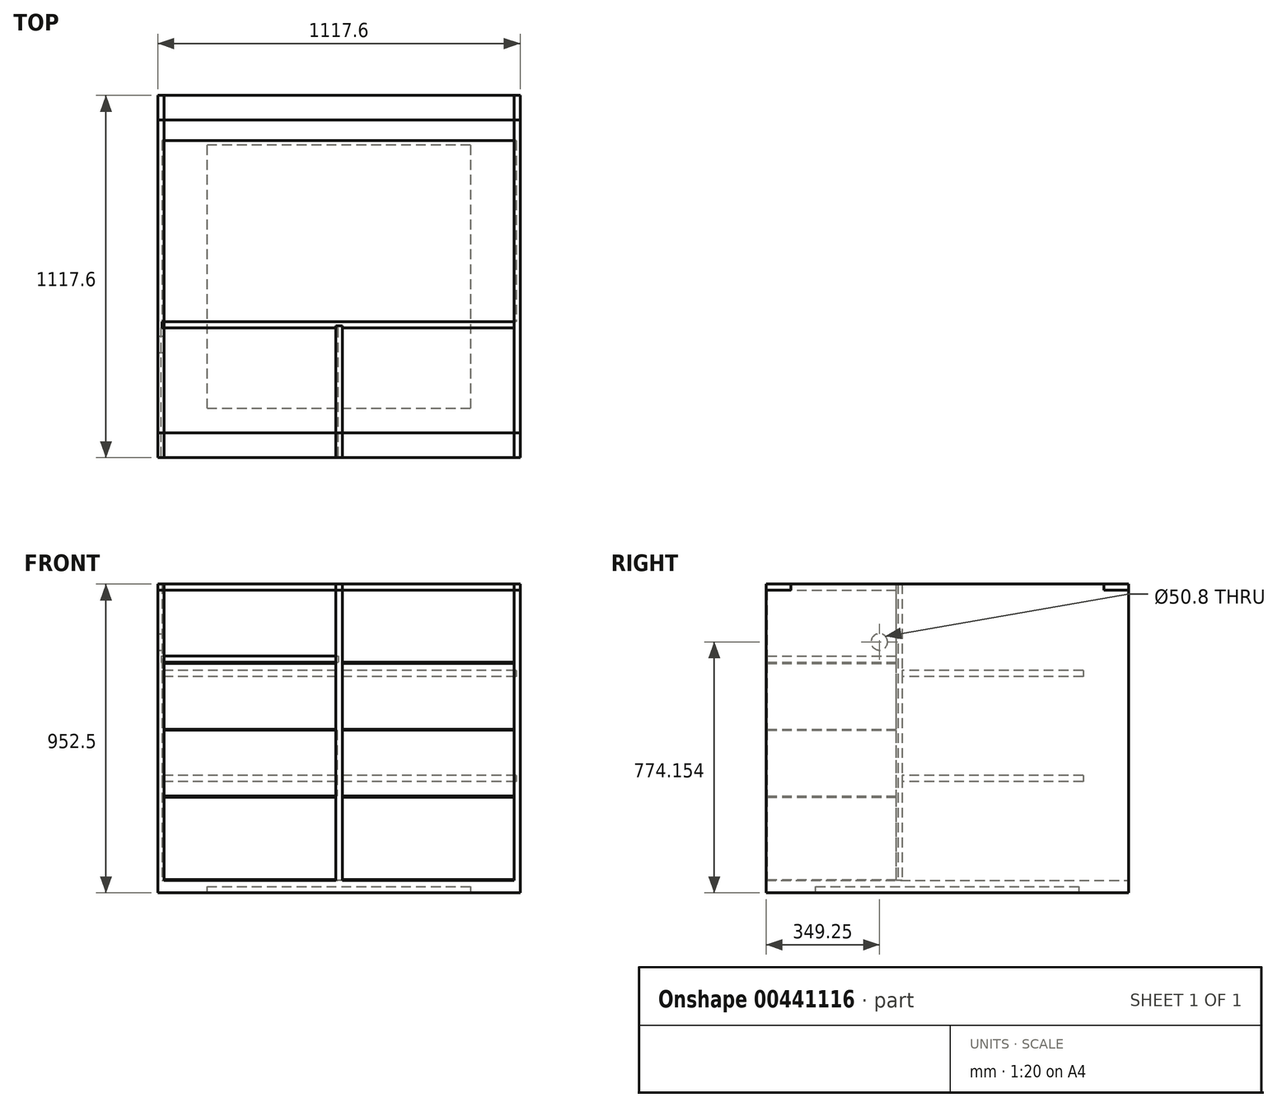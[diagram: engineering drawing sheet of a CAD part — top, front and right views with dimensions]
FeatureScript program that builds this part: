
annotation { "Feature Type Name" : "Feature", "Feature Type Description" : "" }
export const myFeature = defineFeature(function(context is Context, id is Id, definition is map)
    precondition{}
    {
        {
            var Q0;
            Q0=qCreatedBy(makeId("Front.planeOp"),FACE);
            var sketch = newSketch(context, id + "F0", { "sketchPlane" : qUnion([Q0])});
            skLineSegment(sketch, "E0.bottom", {"start": v(-558.8, -457.2) * mm, "end": v(558.8, -457.2) * mm});
            skLineSegment(sketch, "E0.top", {"start": v(-558.8, -476.25) * mm, "end": v(558.8, -476.25) * mm});
            skLineSegment(sketch, "E0.left", {"start": v(-558.8, -457.2) * mm, "end": v(-558.8, -476.25) * mm});
            skLineSegment(sketch, "E0.right", {"start": v(558.8, -457.2) * mm, "end": v(558.8, -476.25) * mm});
            skSolve(sketch);
        }
        {
            var Q0;
            Q0=qCreatedBy(makeId("Front.planeOp"),FACE);
            var sketch = newSketch(context, id + "F1", { "sketchPlane" : qUnion([Q0])});
            skLineSegment(sketch, "E1.bottom", {"start": v(-539.75, 457.2) * mm, "end": v(-558.8, 457.2) * mm});
            skLineSegment(sketch, "E1.top", {"start": v(-539.75, -457.2) * mm, "end": v(-558.8, -457.2) * mm});
            skLineSegment(sketch, "E1.left", {"start": v(-539.75, 457.2) * mm, "end": v(-539.75, -457.2) * mm});
            skLineSegment(sketch, "E1.right", {"start": v(-558.8, 457.2) * mm, "end": v(-558.8, -457.2) * mm});
            skSolve(sketch);
        }
        {
            var Q0;
            Q0=qCreatedBy(makeId("Front.planeOp"),FACE);
            var sketch = newSketch(context, id + "F2", { "sketchPlane" : qUnion([Q0])});
            skLineSegment(sketch, "E2.bottom", {"start": v(539.75, 457.2) * mm, "end": v(558.8, 457.2) * mm});
            skLineSegment(sketch, "E2.top", {"start": v(539.75, -457.2) * mm, "end": v(558.8, -457.2) * mm});
            skLineSegment(sketch, "E2.left", {"start": v(539.75, 457.2) * mm, "end": v(539.75, -457.2) * mm});
            skLineSegment(sketch, "E2.right", {"start": v(558.8, 457.2) * mm, "end": v(558.8, -457.2) * mm});
            skSolve(sketch);
        }
        {
            var Q0;
            Q0 = qSketchRegion(id + "F1", true);
            extrude(context, id + "F3", {"entities" : qUnion([Q0]), "depth" : 558.8 * mm, "hasSecondDirection" : true, "secondDirectionOppositeDirection" : true, "secondDirectionDepth" : 558.8 * mm});
        }
        {
            var Q0;
            Q0 = qSketchRegion(id + "F2", true);
            extrude(context, id + "F4", {"entities" : qUnion([Q0]), "depth" : 558.8 * mm, "hasSecondDirection" : true, "secondDirectionOppositeDirection" : true, "secondDirectionDepth" : 558.8 * mm});
        }
        {
            var Q0;
            Q0 = qSketchRegion(id + "F0", true);
            extrude(context, id + "F5", {"entities" : qUnion([Q0]), "operationType" : NewBodyOperationType.ADD, "depth" : 558.8 * mm, "hasSecondDirection" : true, "secondDirectionOppositeDirection" : true, "secondDirectionDepth" : 558.8 * mm});
        }
        {
            var Q0;
            Q0=qCreatedBy(makeId("Right.planeOp"),FACE);
            var sketch = newSketch(context, id + "F6", { "sketchPlane" : qUnion([Q0])});
            skLineSegment(sketch, "E3.bottom", {"start": v(-558.8, 457.2) * mm, "end": v(-152.4, 457.2) * mm});
            skLineSegment(sketch, "E3.top", {"start": v(-558.8, -457.2) * mm, "end": v(-152.4, -457.2) * mm});
            skLineSegment(sketch, "E3.left", {"start": v(-558.8, 457.2) * mm, "end": v(-558.8, -457.2) * mm});
            skLineSegment(sketch, "E3.right", {"start": v(-152.4, 457.2) * mm, "end": v(-152.4, -457.2) * mm});
            skSolve(sketch);
        }
        {
            var Q0;
            Q0 = qSketchRegion(id + "F6", true);
            extrude(context, id + "F7", {"entities" : qUnion([Q0]), "operationType" : NewBodyOperationType.ADD, "depth" : 9.84 * mm, "hasSecondDirection" : true, "secondDirectionOppositeDirection" : true, "secondDirectionDepth" : 9.84 * mm});
        }
        {
            var Q0;
            Q0=makeQuery(id+"F3.opExtrude","SWEPT_FACE",FACE,{"disambiguationData":[OSD([sQuery(id+"F1.wireOp",EDGE,"E1.right")])]});
            var sketch = newSketch(context, id + "F8", { "sketchPlane" : qUnion([Q0])});
            skLineSegment(sketch, "E4.bottom", {"start": v(-558.8, 457.2) * mm, "end": v(-482.6, 457.2) * mm});
            skLineSegment(sketch, "E4.top", {"start": v(-558.8, 438.15) * mm, "end": v(-482.6, 438.15) * mm});
            skLineSegment(sketch, "E4.left", {"start": v(-558.8, 457.2) * mm, "end": v(-558.8, 438.15) * mm});
            skLineSegment(sketch, "E4.right", {"start": v(-482.6, 457.2) * mm, "end": v(-482.6, 438.15) * mm});
            skLineSegment(sketch, "E5.bottom", {"start": v(558.8, 457.2) * mm, "end": v(482.6, 457.2) * mm});
            skLineSegment(sketch, "E5.top", {"start": v(558.8, 438.15) * mm, "end": v(482.6, 438.15) * mm});
            skLineSegment(sketch, "E5.left", {"start": v(558.8, 457.2) * mm, "end": v(558.8, 438.15) * mm});
            skLineSegment(sketch, "E5.right", {"start": v(482.6, 457.2) * mm, "end": v(482.6, 438.15) * mm});
            skSolve(sketch);
        }
        {
            var Q0;
            Q0 = qSketchRegion(id + "F8", true);
            extrude(context, id + "F9", {"entities" : qUnion([Q0]), "depth" : -1117.6 * mm});
        }
        {
            var Q0;
            Q0=makeQuery(id+"F5.opExtrude","SWEPT_FACE",FACE,{"disambiguationData":[OSD([sQuery(id+"F0.wireOp",EDGE,"E0.bottom")])]});
            var sketch = newSketch(context, id + "F10", { "sketchPlane" : qUnion([Q0])});
            skLineSegment(sketch, "E6.bottom", {"start": v(-546.1, -139.7) * mm, "end": v(552.45, -139.7) * mm});
            skLineSegment(sketch, "E6.top", {"start": v(-546.1, -158.75) * mm, "end": v(552.45, -158.75) * mm});
            skLineSegment(sketch, "E6.left", {"start": v(-546.1, -139.7) * mm, "end": v(-546.1, -158.75) * mm});
            skLineSegment(sketch, "E6.right", {"start": v(552.45, -139.7) * mm, "end": v(552.45, -158.75) * mm});
            skSolve(sketch);
        }
        {
            var Q0;
            {var subQ0=sQuery(id+"F10.wireOp",EDGE,"E6.left");Q0=makeQuery(id+"F10.imprint","IMPRINT",FACE,{"disambiguationData":[TD([[makeQuery(id+"F10.imprint","IMPRINT",EDGE,{"derivedFrom":subQ0}),1.0]])]});}
            extrude(context, id + "F11", {"entities" : qUnion([Q0]), "depth" : 914.4 * mm});
        }
        {
            var Q0;
            Q0=makeQuery(id+"F5.opExtrude","SWEPT_FACE",FACE,{"disambiguationData":[OSD([sQuery(id+"F0.wireOp",EDGE,"E0.top")])]});
            var sketch = newSketch(context, id + "F12", { "sketchPlane" : qUnion([Q0])});
            skLineSegment(sketch, "E7.bottom", {"start": v(-558.8, 558.8) * mm, "end": v(558.8, 558.8) * mm});
            skLineSegment(sketch, "E7.top", {"start": v(-558.8, -558.8) * mm, "end": v(558.8, -558.8) * mm});
            skLineSegment(sketch, "E7.left", {"start": v(-558.8, 558.8) * mm, "end": v(-558.8, -558.8) * mm});
            skLineSegment(sketch, "E7.right", {"start": v(558.8, 558.8) * mm, "end": v(558.8, -558.8) * mm});
            skLineSegment(sketch, "E8.0", {"start": v(-406.4, 406.4) * mm, "end": v(-406.4, -406.4) * mm});
            skLineSegment(sketch, "E8.1", {"start": v(-406.4, 406.4) * mm, "end": v(406.4, 406.4) * mm});
            skLineSegment(sketch, "E8.2", {"start": v(406.4, 406.4) * mm, "end": v(406.4, -406.4) * mm});
            skLineSegment(sketch, "E8.3", {"start": v(-406.4, -406.4) * mm, "end": v(406.4, -406.4) * mm});
            skSolve(sketch);
        }
        {
            var Q0;
            Q0 = qSketchRegion(id + "F12", true);
            extrude(context, id + "F13", {"entities" : qUnion([Q0]), "operationType" : NewBodyOperationType.ADD, "depth" : 19.05 * mm});
        }
        {
            var Q0;
            {var subQ0=sQuery(id+"F10.wireOp",EDGE,"E6.top");Q0=makeQuery(id+"F11.opExtrude","SWEPT_FACE",FACE,{"disambiguationData":[OSD([subQ0]),TDD([makeQuery(id+"F10.imprint","IMPRINT",EDGE,{"disambiguationData":[TD([[makeQuery(id+"F10.imprint","INTERSECT",VERTEX,{"derivedFrom":[subQ0,sQuery(id+"F10.wireOp",EDGE,"E6.left")]}),-1.0]])],"derivedFrom":subQ0})])]});}
            var sketch = newSketch(context, id + "F14", { "sketchPlane" : qUnion([Q0])});
            skLineSegment(sketch, "E9.bottom", {"start": v(-548.96, 234.95) * mm, "end": v(-2.86, 234.95) * mm});
            skLineSegment(sketch, "E9.top", {"start": v(-548.96, 215.9) * mm, "end": v(-2.86, 215.9) * mm});
            skLineSegment(sketch, "E9.left", {"start": v(-548.96, 234.95) * mm, "end": v(-548.96, 215.9) * mm});
            skLineSegment(sketch, "E9.right", {"start": v(-2.86, 234.95) * mm, "end": v(-2.86, 215.9) * mm});
            skSolve(sketch);
        }
        {
            var Q0;
            Q0 = qSketchRegion(id + "F14", true);
            extrude(context, id + "F15", {"entities" : qUnion([Q0]), "depth" : 396.88 * mm});
        }
        {
            var Q0;
            Q0=makeQuery(id+"F3.opExtrude","SWEPT_FACE",FACE,{"disambiguationData":[OSD([sQuery(id+"F1.wireOp",EDGE,"E1.left")])]});
            var sketch = newSketch(context, id + "F16", { "sketchPlane" : qUnion([Q0])});
            skLineSegment(sketch, "E10.bottom", {"start": v(-158.75, 228.05) * mm, "end": v(-209.55, 228.05) * mm});
            skLineSegment(sketch, "E10.top", {"start": v(-158.75, 278.85) * mm, "end": v(-209.55, 278.85) * mm});
            skLineSegment(sketch, "E10.left", {"start": v(-158.75, 228.05) * mm, "end": v(-158.75, 278.85) * mm});
            skLineSegment(sketch, "E10.right", {"start": v(-209.55, 228.05) * mm, "end": v(-209.55, 278.85) * mm});
            skCircle(sketch, "E11", {"center": v(-209.55, 278.85) * mm, "radius": 25.4 * mm});
            skSolve(sketch);
        }
        {
            var Q0;
            Q0=sQuery(id+"F16.wireOp",VERTEX,"E10.top.end");
            var Q1;
            Q1=makeQuery(id+"F3.opExtrude","SWEPT_BODY",BODY,{"disambiguationData":[OSD([sQuery(id+"F1.wireOp",EDGE,"E1.bottom"),sQuery(id+"F1.wireOp",EDGE,"E1.top"),sQuery(id+"F1.wireOp",EDGE,"E1.left"),sQuery(id+"F1.wireOp",EDGE,"E1.right")])]});
            hole(context, id + "F17", {"style" : HoleStyle.SIMPLE, "endStyle" : HoleEndStyle.BLIND, "holeDiameter" : 50.8 * mm, "holeDepth" : 25.4 * mm, "isTappedThrough" : true, "tappedDepth" : 12.7 * mm, "tapClearance" : 3, "locations" : qUnion([Q0]), "scope" : qUnion([Q1])});
        }
        {
            var Q0;
            {var subQ0=sQuery(id+"F10.wireOp",EDGE,"E6.top");Q0=makeQuery(id+"F11.opExtrude","SWEPT_FACE",FACE,{"disambiguationData":[OSD([subQ0]),TDD([makeQuery(id+"F10.imprint","IMPRINT",EDGE,{"disambiguationData":[TD([[makeQuery(id+"F10.imprint","INTERSECT",VERTEX,{"derivedFrom":[subQ0,sQuery(id+"F10.wireOp",EDGE,"E6.left")]}),-1.0]])],"derivedFrom":subQ0})])]});}
            var sketch = newSketch(context, id + "F18", { "sketchPlane" : qUnion([Q0])});
            skLineSegment(sketch, "E12.bottom", {"start": v(-539.75, 212.72) * mm, "end": v(-9.84, 212.72) * mm});
            skLineSegment(sketch, "E12.top", {"start": v(-539.75, 9.52) * mm, "end": v(-9.84, 9.52) * mm});
            skLineSegment(sketch, "E12.left", {"start": v(-539.75, 212.72) * mm, "end": v(-539.75, 9.52) * mm});
            skLineSegment(sketch, "E12.right", {"start": v(-9.84, 212.72) * mm, "end": v(-9.84, 9.52) * mm});
            skSolve(sketch);
        }
        {
            var Q0;
            Q0 = qSketchRegion(id + "F18", true);
            extrude(context, id + "F19", {"entities" : qUnion([Q0]), "depth" : 396.88 * mm});
        }
        {
            var Q0;
            {var subQ0=sQuery(id+"F10.wireOp",EDGE,"E6.top");Q0=makeQuery(id+"F11.opExtrude","SWEPT_FACE",FACE,{"disambiguationData":[OSD([subQ0]),TDD([makeQuery(id+"F10.imprint","IMPRINT",EDGE,{"disambiguationData":[TD([[makeQuery(id+"F10.imprint","INTERSECT",VERTEX,{"derivedFrom":[subQ0,sQuery(id+"F10.wireOp",EDGE,"E6.left")]}),-1.0]])],"derivedFrom":subQ0})])]});}
            var sketch = newSketch(context, id + "F20", { "sketchPlane" : qUnion([Q0])});
            skLineSegment(sketch, "E13.bottom", {"start": v(-9.84, 236.5) * mm, "end": v(-60.64, 236.5) * mm});
            skLineSegment(sketch, "E13.top", {"start": v(-9.84, 287.3) * mm, "end": v(-60.64, 287.3) * mm});
            skLineSegment(sketch, "E13.left", {"start": v(-9.84, 236.5) * mm, "end": v(-9.84, 287.3) * mm});
            skLineSegment(sketch, "E13.right", {"start": v(-60.64, 236.5) * mm, "end": v(-60.64, 287.3) * mm});
            skCircle(sketch, "E14", {"center": v(-60.64, 287.3) * mm, "radius": 25.4 * mm});
            skSolve(sketch);
        }
        {
            var Q0;
            Q0=sQuery(id+"F20.wireOp",VERTEX,"E14.center");
            var Q1;
            Q1=makeQuery(id+"F11.opExtrude","SWEPT_BODY",BODY,{"disambiguationData":[OSD([sQuery(id+"F2.wireOp",EDGE,"E2.top"),sQuery(id+"F2.wireOp",EDGE,"E2.left"),sQuery(id+"F6.wireOp",EDGE,"E3.top"),sQuery(id+"F6.wireOp",EDGE,"E3.right"),sQuery(id+"F10.wireOp",EDGE,"E6.bottom"),sQuery(id+"F10.wireOp",EDGE,"E6.top"),sQuery(id+"F10.wireOp",EDGE,"E6.left")])]});
            hole(context, id + "F21", {"style" : HoleStyle.SIMPLE, "endStyle" : HoleEndStyle.BLIND, "holeDiameter" : 50.8 * mm, "holeDepth" : 25.4 * mm, "isTappedThrough" : true, "tappedDepth" : 12.7 * mm, "tapClearance" : 3, "locations" : qUnion([Q0]), "scope" : qUnion([Q1])});
        }
        {
            var Q0;
            {var subQ0=sQuery(id+"F10.wireOp",EDGE,"E6.top");Q0=makeQuery(id+"F11.opExtrude","SWEPT_FACE",FACE,{"disambiguationData":[OSD([subQ0]),TDD([makeQuery(id+"F10.imprint","IMPRINT",EDGE,{"disambiguationData":[TD([[makeQuery(id+"F10.imprint","INTERSECT",VERTEX,{"derivedFrom":[subQ0,sQuery(id+"F10.wireOp",EDGE,"E6.left")]}),-1.0]])],"derivedFrom":subQ0})])]});}
            var sketch = newSketch(context, id + "F22", { "sketchPlane" : qUnion([Q0])});
            skLineSegment(sketch, "E15.bottom", {"start": v(-539.75, 6.35) * mm, "end": v(-6.35, 6.35) * mm});
            skLineSegment(sketch, "E15.top", {"start": v(-539.75, -196.85) * mm, "end": v(-6.35, -196.85) * mm});
            skLineSegment(sketch, "E15.left", {"start": v(-539.75, 6.35) * mm, "end": v(-539.75, -196.85) * mm});
            skLineSegment(sketch, "E15.right", {"start": v(-6.35, 6.35) * mm, "end": v(-6.35, -196.85) * mm});
            skSolve(sketch);
        }
        {
            var Q0;
            Q0 = qSketchRegion(id + "F22", true);
            extrude(context, id + "F23", {"entities" : qUnion([Q0]), "depth" : 396.88 * mm});
        }
        {
            var Q0;
            {var subQ0=sQuery(id+"F10.wireOp",EDGE,"E6.top");Q0=makeQuery(id+"F11.opExtrude","SWEPT_FACE",FACE,{"disambiguationData":[OSD([subQ0]),TDD([makeQuery(id+"F10.imprint","IMPRINT",EDGE,{"disambiguationData":[TD([[makeQuery(id+"F10.imprint","INTERSECT",VERTEX,{"derivedFrom":[subQ0,sQuery(id+"F10.wireOp",EDGE,"E6.left")]}),-1.0]])],"derivedFrom":subQ0})])]});}
            var sketch = newSketch(context, id + "F24", { "sketchPlane" : qUnion([Q0])});
            skLineSegment(sketch, "E16.bottom", {"start": v(-539.75, -200.03) * mm, "end": v(-9.84, -200.03) * mm});
            skLineSegment(sketch, "E16.top", {"start": v(-539.75, -454.03) * mm, "end": v(-9.84, -454.03) * mm});
            skLineSegment(sketch, "E16.left", {"start": v(-539.75, -200.03) * mm, "end": v(-539.75, -454.03) * mm});
            skLineSegment(sketch, "E16.right", {"start": v(-9.84, -200.03) * mm, "end": v(-9.84, -454.03) * mm});
            skLineSegment(sketch, "E17.bottom", {"start": v(9.84, -200.03) * mm, "end": v(539.75, -200.03) * mm});
            skLineSegment(sketch, "E17.top", {"start": v(9.84, -454.03) * mm, "end": v(539.75, -454.03) * mm});
            skLineSegment(sketch, "E17.left", {"start": v(9.84, -200.03) * mm, "end": v(9.84, -454.03) * mm});
            skLineSegment(sketch, "E17.right", {"start": v(539.75, -200.03) * mm, "end": v(539.75, -454.03) * mm});
            skLineSegment(sketch, "E18.bottom", {"start": v(9.84, 6.35) * mm, "end": v(539.75, 6.35) * mm});
            skLineSegment(sketch, "E18.top", {"start": v(9.84, -196.85) * mm, "end": v(539.75, -196.85) * mm});
            skLineSegment(sketch, "E18.left", {"start": v(9.84, 6.35) * mm, "end": v(9.84, -196.85) * mm});
            skLineSegment(sketch, "E18.right", {"start": v(539.75, 6.35) * mm, "end": v(539.75, -196.85) * mm});
            skLineSegment(sketch, "E19.bottom", {"start": v(9.2, 212.72) * mm, "end": v(539.75, 212.72) * mm});
            skLineSegment(sketch, "E19.top", {"start": v(9.2, 9.52) * mm, "end": v(539.75, 9.52) * mm});
            skLineSegment(sketch, "E19.left", {"start": v(9.2, 212.72) * mm, "end": v(9.2, 9.52) * mm});
            skLineSegment(sketch, "E19.right", {"start": v(539.75, 212.72) * mm, "end": v(539.75, 9.52) * mm});
            skLineSegment(sketch, "E20.bottom", {"start": v(9.84, 438.15) * mm, "end": v(539.75, 438.15) * mm});
            skLineSegment(sketch, "E20.top", {"start": v(9.84, 215.9) * mm, "end": v(539.75, 215.9) * mm});
            skLineSegment(sketch, "E20.left", {"start": v(9.84, 438.15) * mm, "end": v(9.84, 215.9) * mm});
            skLineSegment(sketch, "E20.right", {"start": v(539.75, 438.15) * mm, "end": v(539.75, 215.9) * mm});
            skSolve(sketch);
        }
        {
            var Q0;
            Q0 = qSketchRegion(id + "F24", true);
            extrude(context, id + "F25", {"entities" : qUnion([Q0]), "depth" : 396.88 * mm});
        }
        {
            var Q0;
            Q0=makeQuery(id+"F11.opExtrude","SWEPT_FACE",FACE,{"disambiguationData":[OSD([sQuery(id+"F10.wireOp",EDGE,"E6.bottom")])]});
            var sketch = newSketch(context, id + "F26", { "sketchPlane" : qUnion([Q0])});
            skLineSegment(sketch, "E21.bottom", {"start": v(-546.1, 190.5) * mm, "end": v(546.1, 190.5) * mm});
            skLineSegment(sketch, "E21.top", {"start": v(-546.1, 171.45) * mm, "end": v(546.1, 171.45) * mm});
            skLineSegment(sketch, "E21.left", {"start": v(-546.1, 190.5) * mm, "end": v(-546.1, 171.45) * mm});
            skLineSegment(sketch, "E21.right", {"start": v(546.1, 190.5) * mm, "end": v(546.1, 171.45) * mm});
            skLineSegment(sketch, "E22.bottom", {"start": v(-546.1, -133.35) * mm, "end": v(546.1, -133.35) * mm});
            skLineSegment(sketch, "E22.top", {"start": v(-546.1, -152.4) * mm, "end": v(546.1, -152.4) * mm});
            skLineSegment(sketch, "E22.left", {"start": v(-546.1, -133.35) * mm, "end": v(-546.1, -152.4) * mm});
            skLineSegment(sketch, "E22.right", {"start": v(546.1, -133.35) * mm, "end": v(546.1, -152.4) * mm});
            skSolve(sketch);
        }
        {
            var Q0;
            Q0 = qSketchRegion(id + "F26", true);
            extrude(context, id + "F27", {"entities" : qUnion([Q0]), "depth" : 558.8 * mm});
        }
    });
